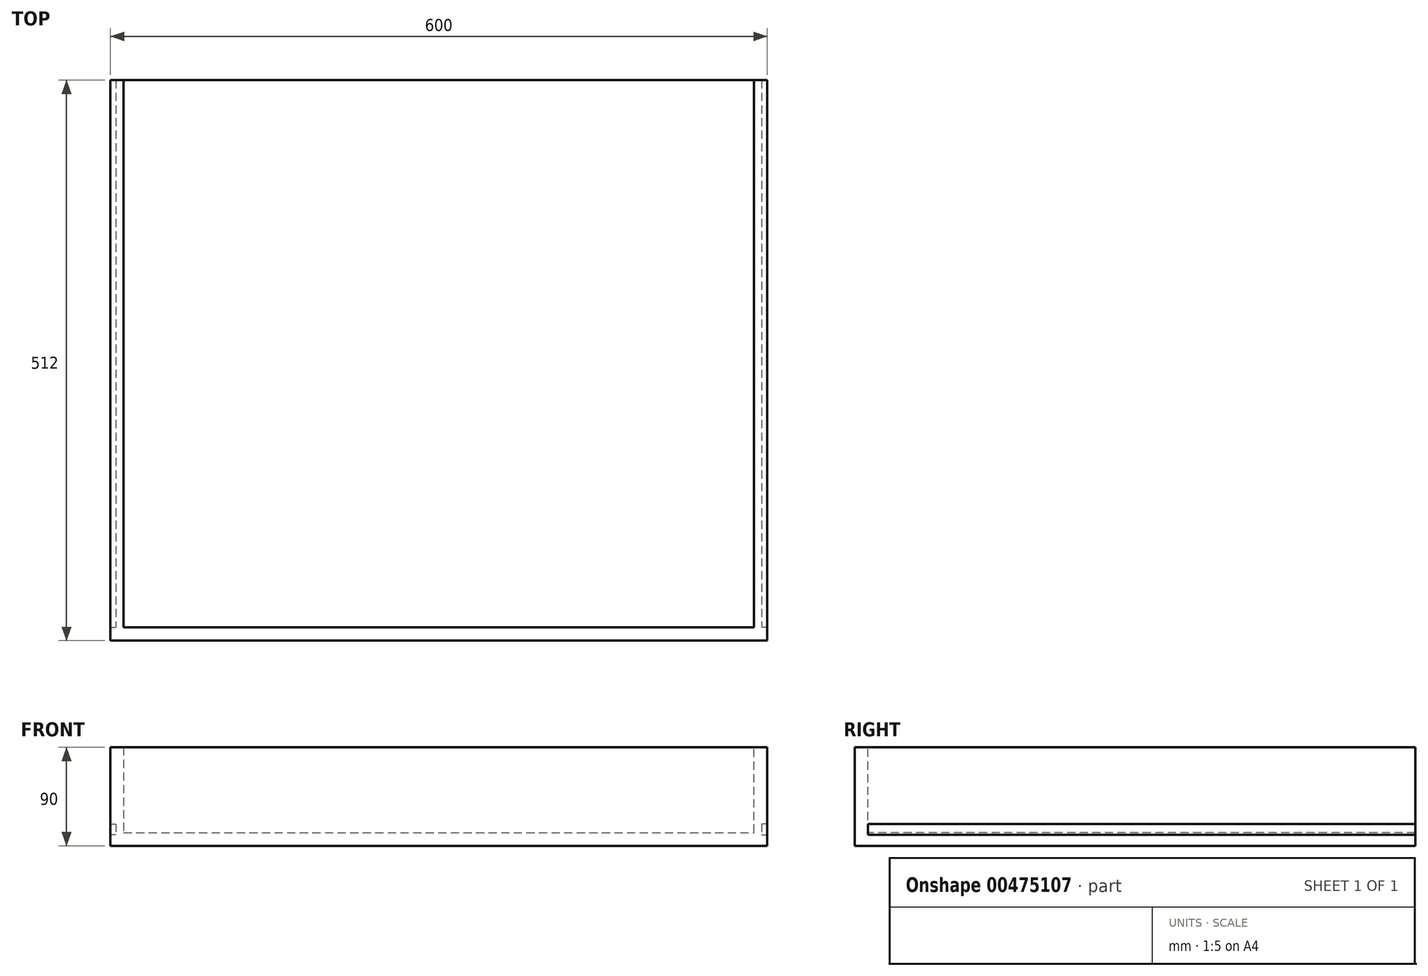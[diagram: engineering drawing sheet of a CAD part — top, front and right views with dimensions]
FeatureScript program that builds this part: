
annotation { "Feature Type Name" : "Feature", "Feature Type Description" : "" }
export const myFeature = defineFeature(function(context is Context, id is Id, definition is map)
    precondition{}
    {
        {
            var Q0;
            Q0=qCreatedBy(makeId("Front.planeOp"),FACE);
            var sketch = newSketch(context, id + "F0", { "sketchPlane" : qUnion([Q0])});
            skLineSegment(sketch, "E0.bottom", {"start": v(-300, 90) * mm, "end": v(300, 90) * mm, "construction": true});
            skLineSegment(sketch, "E0.top", {"start": v(-300, 0) * mm, "end": v(300, 0) * mm, "construction": true});
            skLineSegment(sketch, "E0.left", {"start": v(-300, 90) * mm, "end": v(-300, 0) * mm, "construction": true});
            skLineSegment(sketch, "E0.right", {"start": v(300, 90) * mm, "end": v(300, 0) * mm, "construction": true});
            skLineSegment(sketch, "E1", {"start": v(-300, 12) * mm, "end": v(300, 12) * mm, "construction": true});
            skLineSegment(sketch, "E2", {"start": v(-295, 90) * mm, "end": v(-295, 0) * mm, "construction": true});
            skLineSegment(sketch, "E3", {"start": v(295, 90) * mm, "end": v(295, 0) * mm, "construction": true});
            skLineSegment(sketch, "E4", {"start": v(288, 90) * mm, "end": v(288, 0) * mm, "construction": true});
            skLineSegment(sketch, "E5", {"start": v(-300, 10) * mm, "end": v(300, 10) * mm, "construction": true});
            skLineSegment(sketch, "E6", {"start": v(-300, 20) * mm, "end": v(300, 20) * mm, "construction": true});
            skLineSegment(sketch, "E7", {"start": v(-288, 12) * mm, "end": v(288, 12) * mm});
            skLineSegment(sketch, "E8", {"start": v(300, 0) * mm, "end": v(-300, 0) * mm});
            skLineSegment(sketch, "E9", {"start": v(-300, 90) * mm, "end": v(-300, 20) * mm});
            skLineSegment(sketch, "E10", {"start": v(-295, 20) * mm, "end": v(-295, 10) * mm});
            skLineSegment(sketch, "E11", {"start": v(-295, 10) * mm, "end": v(-300, 10) * mm});
            skLineSegment(sketch, "E12", {"start": v(-300, 20) * mm, "end": v(-295, 20) * mm});
            skLineSegment(sketch, "E13", {"start": v(-300, 10) * mm, "end": v(-300, 0) * mm});
            skLineSegment(sketch, "E14", {"start": v(-300, 90) * mm, "end": v(-288, 90) * mm});
            skLineSegment(sketch, "E15", {"start": v(288, 12) * mm, "end": v(288, 90) * mm});
            skLineSegment(sketch, "E16", {"start": v(288, 90) * mm, "end": v(300, 90) * mm});
            skLineSegment(sketch, "E17", {"start": v(300, 90) * mm, "end": v(300, 20) * mm});
            skLineSegment(sketch, "E18", {"start": v(300, 20) * mm, "end": v(295, 20) * mm});
            skLineSegment(sketch, "E19", {"start": v(295, 10) * mm, "end": v(300, 10) * mm});
            skLineSegment(sketch, "E20", {"start": v(295, 20) * mm, "end": v(295, 10) * mm});
            skLineSegment(sketch, "E21", {"start": v(300, 10) * mm, "end": v(300, 0) * mm});
            skLineSegment(sketch, "E22", {"start": v(-288, 0) * mm, "end": v(-288, 90) * mm, "construction": true});
            skLineSegment(sketch, "E23", {"start": v(-288, 90) * mm, "end": v(-288, 12) * mm});
            skSolve(sketch);
        }
        {
            var Q0;
            Q0 = qSketchRegion(id + "F0", true);
            extrude(context, id + "F1", {"entities" : qUnion([Q0]), "oppositeDirection" : true, "depth" : 500 * mm});
        }
        {
            var Q0;
            Q0=qCreatedBy(makeId("Front.planeOp"),FACE);
            var sketch = newSketch(context, id + "F2", { "sketchPlane" : qUnion([Q0])});
            skLineSegment(sketch, "E24.bottom", {"start": v(-300, 90) * mm, "end": v(300, 90) * mm});
            skLineSegment(sketch, "E24.top", {"start": v(-300, 0) * mm, "end": v(300, 0) * mm});
            skLineSegment(sketch, "E24.left", {"start": v(-300, 90) * mm, "end": v(-300, 0) * mm});
            skLineSegment(sketch, "E24.right", {"start": v(300, 90) * mm, "end": v(300, 0) * mm});
            skSolve(sketch);
        }
        {
            var Q0;
            Q0 = qSketchRegion(id + "F2", true);
            extrude(context, id + "F3", {"entities" : qUnion([Q0]), "operationType" : NewBodyOperationType.ADD, "depth" : 12 * mm});
        }
    });
